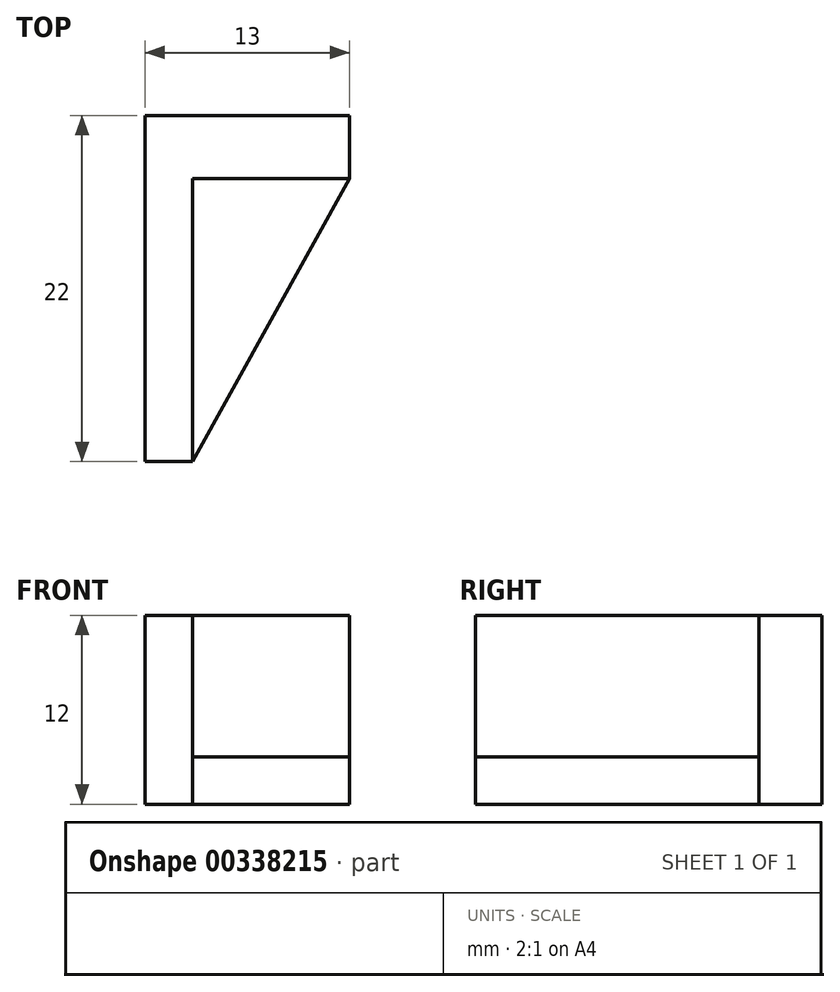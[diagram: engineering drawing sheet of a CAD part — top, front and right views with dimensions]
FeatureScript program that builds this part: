
annotation { "Feature Type Name" : "Feature", "Feature Type Description" : "" }
export const myFeature = defineFeature(function(context is Context, id is Id, definition is map)
    precondition{}
    {
        {
            var Q0;
            Q0=qCreatedBy(makeId("Top.planeOp"),FACE);
            var sketch = newSketch(context, id + "F0", { "sketchPlane" : qUnion([Q0])});
            skLineSegment(sketch, "E0.bottom", {"start": v(0, 0) * mm, "end": v(13, 0) * mm});
            skLineSegment(sketch, "E0.top", {"start": v(0, -22) * mm, "end": v(13, -22) * mm});
            skLineSegment(sketch, "E0.left", {"start": v(0, 0) * mm, "end": v(0, -22) * mm});
            skLineSegment(sketch, "E0.right", {"start": v(13, 0) * mm, "end": v(13, -22) * mm});
            skSolve(sketch);
        }
        {
            var Q0;
            Q0 = qSketchRegion(id + "F0", true);
            extrude(context, id + "F1", {"entities" : qUnion([Q0]), "depth" : 12 * mm});
        }
        {
            var Q0;
            Q0=makeQuery(id+"F1.opExtrude","CAP_FACE",FACE,{"disambiguationData":[OSD([sQuery(id+"F0.wireOp",EDGE,"E0.bottom"),sQuery(id+"F0.wireOp",EDGE,"E0.top"),sQuery(id+"F0.wireOp",EDGE,"E0.left"),sQuery(id+"F0.wireOp",EDGE,"E0.right")])],"isStart":false});
            var sketch = newSketch(context, id + "F2", { "sketchPlane" : qUnion([Q0])});
            skLineSegment(sketch, "E1", {"start": v(13, -4) * mm, "end": v(13, -22) * mm});
            skLineSegment(sketch, "E2", {"start": v(13, -22) * mm, "end": v(3, -22) * mm});
            skLineSegment(sketch, "E3", {"start": v(3, -22) * mm, "end": v(13, -4) * mm});
            skSolve(sketch);
        }
        {
            var Q0;
            Q0 = qSketchRegion(id + "F2", true);
            extrude(context, id + "F3", {"entities" : qUnion([Q0]), "operationType" : NewBodyOperationType.REMOVE, "endBound" : BoundingType.THROUGH_ALL, "oppositeDirection" : true, "depth" : 25 * mm});
        }
        {
            var Q0;
            Q0=makeQuery(id+"F1.opExtrude","CAP_FACE",FACE,{"disambiguationData":[OSD([sQuery(id+"F0.wireOp",EDGE,"E0.bottom"),sQuery(id+"F0.wireOp",EDGE,"E0.top"),sQuery(id+"F0.wireOp",EDGE,"E0.left"),sQuery(id+"F0.wireOp",EDGE,"E0.right")])],"isStart":false});
            var sketch = newSketch(context, id + "F4", { "sketchPlane" : qUnion([Q0])});
            skLineSegment(sketch, "E4", {"start": v(3, -22) * mm, "end": v(3, -4) * mm});
            skLineSegment(sketch, "E5", {"start": v(3, -4) * mm, "end": v(13, -4) * mm});
            skLineSegment(sketch, "E6", {"start": v(13, -4) * mm, "end": v(3, -22) * mm});
            skSolve(sketch);
        }
        {
            var Q0;
            Q0 = qSketchRegion(id + "F4", true);
            extrude(context, id + "F5", {"entities" : qUnion([Q0]), "operationType" : NewBodyOperationType.REMOVE, "oppositeDirection" : true, "depth" : 9 * mm});
        }
    });
